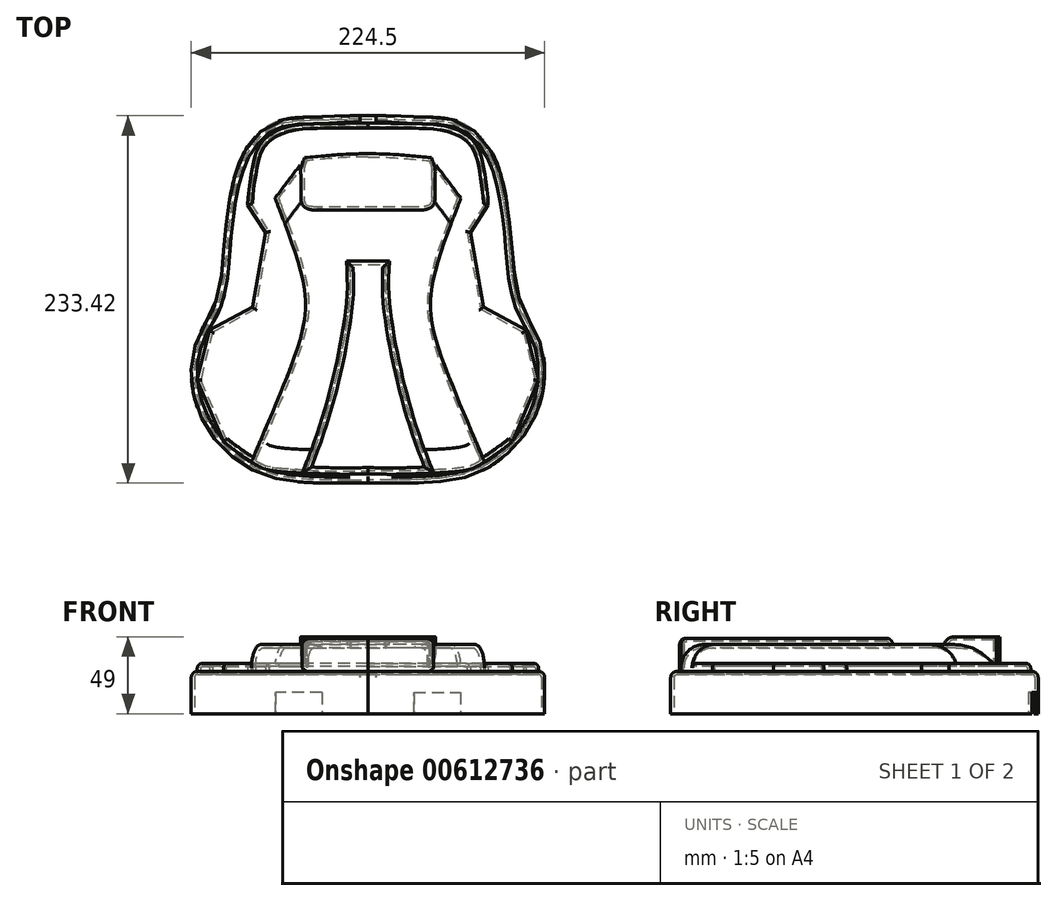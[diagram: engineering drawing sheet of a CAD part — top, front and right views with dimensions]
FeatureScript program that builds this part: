
annotation { "Feature Type Name" : "Feature", "Feature Type Description" : "" }
export const myFeature = defineFeature(function(context is Context, id is Id, definition is map)
    precondition{}
    {
        {
            var Q0;
            Q0=qCreatedBy(makeId("Top.planeOp"),FACE);
            var sketch = newSketch(context, id + "F0", { "sketchPlane" : qUnion([Q0])});
            skFitSpline(sketch, "E0", {"points": [v(0, 119.05) * mm, v(-30.72, 118.24) * mm, v(-55.15, 116.1) * mm, v(-69.4, 106.9) * mm, v(-80.35, 89.32) * mm, v(-88.63, 47.3) * mm, v(-91.91, 14.02) * mm, v(-96.74, -3.06) * mm, v(-101.1, -10.8) * mm, v(-108.33, -26.62) * mm, v(-110.21, -43.05) * mm, v(-107.64, -60) * mm, v(-100.19, -76.77) * mm, v(-92.8, -86.72) * mm, v(-84.5, -94.37) * mm, v(-62.4, -106.34) * mm, v(0, -110.2) * mm], "startDerivative": vector(-744.36, 0) * mm, "endDerivative": vector(685.33, 9.02) * mm});
            skFitSpline(sketch, "E1.MirrorCS", {"points": [v(0, 119.05) * mm, v(30.72, 118.24) * mm, v(55.15, 116.1) * mm, v(69.4, 106.9) * mm, v(80.35, 89.32) * mm, v(88.63, 47.3) * mm, v(91.91, 14.02) * mm, v(96.74, -3.06) * mm, v(101.1, -10.8) * mm, v(108.33, -26.62) * mm, v(110.21, -43.05) * mm, v(107.64, -60) * mm, v(100.19, -76.77) * mm, v(92.8, -86.72) * mm, v(84.5, -94.37) * mm, v(62.4, -106.34) * mm, v(0, -110.2) * mm], "startDerivative": vector(744.36, 0) * mm, "endDerivative": vector(-685.33, 9.02) * mm});
            skLineSegment(sketch, "E2", {"start": v(-4.96, 119.03) * mm, "end": v(4.96, 119.03) * mm});
            skLineSegment(sketch, "E3", {"start": v(-11.45, -110.35) * mm, "end": v(15, -110.37) * mm});
            skFitSpline(sketch, "E4", {"points": [v(0, 114.28) * mm, v(-18.36, 114.15) * mm, v(-47.6, 112.7) * mm, v(-55.77, 110.2) * mm, v(-60.12, 108.09) * mm, v(-67.36, 100.84) * mm, v(-71.66, 86.85) * mm, v(-74.01, 70.56) * mm, v(-74.33, 64.92) * mm], "startDerivative": vector(-107.9, -0.71) * mm, "endDerivative": vector(-1.45, -57.59) * mm});
            skFitSpline(sketch, "E5", {"points": [v(-74.33, 64.92) * mm, v(-62.9, 47.38) * mm], "startDerivative": vector(11.44, -17.55) * mm, "endDerivative": vector(11.44, -17.55) * mm});
            skFitSpline(sketch, "E6", {"points": [v(-62.9, 47.38) * mm, v(-71.5, -1.86) * mm], "startDerivative": vector(-8.62, -49.24) * mm, "endDerivative": vector(-8.62, -49.24) * mm});
            skFitSpline(sketch, "E7", {"points": [v(-71.5, -1.86) * mm, v(-98.76, -16.48) * mm], "startDerivative": vector(-27.25, -14.62) * mm, "endDerivative": vector(-27.25, -14.62) * mm});
            skFitSpline(sketch, "E8", {"points": [v(-98.76, -16.48) * mm, v(-106.3, -46.83) * mm], "startDerivative": vector(-7.53, -30.35) * mm, "endDerivative": vector(-7.53, -30.35) * mm});
            skFitSpline(sketch, "E9", {"points": [v(-106.3, -46.83) * mm, v(-90.12, -84.72) * mm], "startDerivative": vector(16.17, -37.88) * mm, "endDerivative": vector(16.17, -37.88) * mm});
            skFitSpline(sketch, "E10", {"points": [v(-90.12, -84.72) * mm, v(-84.53, -89.16) * mm, v(-71.5, -98) * mm, v(-62.4, -102.03) * mm, v(-36.71, -104.14) * mm, v(-18.66, -104.7) * mm, v(0, -104.51) * mm], "startDerivative": vector(41.41, -35.24) * mm, "endDerivative": vector(104.18, 2) * mm});
            skFitSpline(sketch, "E11", {"points": [v(0, 94.84) * mm, v(-38.88, 92.49) * mm], "startDerivative": vector(-38.9, 0.44) * mm, "endDerivative": vector(-38.29, -3.6) * mm});
            skFitSpline(sketch, "E12", {"points": [v(-38.88, 92.49) * mm, v(-56.85, 68.63) * mm], "startDerivative": vector(-17.94, -24.15) * mm, "endDerivative": vector(-17.94, -24.15) * mm});
            skFitSpline(sketch, "E13", {"points": [v(-56.85, 68.63) * mm, v(-38.88, 14.12) * mm, v(-38.88, -11.88) * mm, v(-45.96, -36) * mm, v(-60.7, -72.63) * mm, v(-71.5, -98) * mm], "startDerivative": vector(88.21, -228.17) * mm, "endDerivative": vector(-56.6, -131.92) * mm});
            skFitSpline(sketch, "E14", {"points": [v(-38.88, -104.14) * mm, v(-28.8, -76.77) * mm, v(-18.16, -36.98) * mm, v(-11.45, 5.1) * mm, v(-11.45, 26.6) * mm], "startDerivative": vector(43.74, 111.22) * mm, "endDerivative": vector(-4.53, 97.24) * mm});
            skFitSpline(sketch, "E15", {"points": [v(-11.45, 26.6) * mm, v(0, 26.6) * mm], "startDerivative": vector(11.45, 0) * mm, "endDerivative": vector(11.45, 0) * mm});
            skFitSpline(sketch, "E16.MirrorCS", {"points": [v(11.45, 26.6) * mm, v(0, 26.6) * mm], "startDerivative": vector(-11.45, 0) * mm, "endDerivative": vector(-11.45, 0) * mm});
            skFitSpline(sketch, "E17.MirrorCS", {"points": [v(106.3, -46.83) * mm, v(90.12, -84.72) * mm], "startDerivative": vector(-16.17, -37.88) * mm, "endDerivative": vector(-16.17, -37.88) * mm});
            skFitSpline(sketch, "E18.MirrorCS", {"points": [v(0, 94.84) * mm, v(38.88, 92.49) * mm], "startDerivative": vector(38.9, 0.44) * mm, "endDerivative": vector(38.29, -3.6) * mm});
            skFitSpline(sketch, "E19.MirrorCS", {"points": [v(38.88, 92.49) * mm, v(56.85, 68.63) * mm], "startDerivative": vector(17.94, -24.15) * mm, "endDerivative": vector(17.94, -24.15) * mm});
            skFitSpline(sketch, "E20.MirrorCS", {"points": [v(98.76, -16.48) * mm, v(106.3, -46.83) * mm], "startDerivative": vector(7.53, -30.35) * mm, "endDerivative": vector(7.53, -30.35) * mm});
            skFitSpline(sketch, "E21.MirrorCS", {"points": [v(74.33, 64.92) * mm, v(62.9, 47.38) * mm], "startDerivative": vector(-11.44, -17.55) * mm, "endDerivative": vector(-11.44, -17.55) * mm});
            skFitSpline(sketch, "E22.MirrorCS", {"points": [v(62.9, 47.38) * mm, v(71.5, -1.86) * mm], "startDerivative": vector(8.62, -49.24) * mm, "endDerivative": vector(8.62, -49.24) * mm});
            skFitSpline(sketch, "E23.MirrorCS", {"points": [v(71.5, -1.86) * mm, v(98.76, -16.48) * mm], "startDerivative": vector(27.25, -14.62) * mm, "endDerivative": vector(27.25, -14.62) * mm});
            skFitSpline(sketch, "E24.MirrorCS", {"points": [v(38.88, -104.14) * mm, v(28.8, -76.77) * mm, v(18.16, -36.98) * mm, v(11.45, 5.1) * mm, v(11.45, 26.6) * mm], "startDerivative": vector(-43.74, 111.22) * mm, "endDerivative": vector(4.53, 97.24) * mm});
            skFitSpline(sketch, "E25.MirrorCS", {"points": [v(90.12, -84.72) * mm, v(84.53, -89.16) * mm, v(71.5, -98) * mm, v(62.4, -102.03) * mm, v(36.71, -104.14) * mm, v(18.66, -104.7) * mm, v(0, -104.51) * mm], "startDerivative": vector(-41.41, -35.24) * mm, "endDerivative": vector(-104.18, 2) * mm});
            skFitSpline(sketch, "E26.MirrorCS", {"points": [v(0, 114.28) * mm, v(18.36, 114.15) * mm, v(47.6, 112.7) * mm, v(55.77, 110.2) * mm, v(60.12, 108.09) * mm, v(67.36, 100.84) * mm, v(71.66, 86.85) * mm, v(74.01, 70.56) * mm, v(74.33, 64.92) * mm], "startDerivative": vector(107.9, -0.71) * mm, "endDerivative": vector(1.45, -57.59) * mm});
            skFitSpline(sketch, "E27.MirrorCS", {"points": [v(56.85, 68.63) * mm, v(38.88, 14.12) * mm, v(38.88, -11.88) * mm, v(45.96, -36) * mm, v(60.7, -72.63) * mm, v(71.5, -98) * mm], "startDerivative": vector(-88.21, -228.17) * mm, "endDerivative": vector(56.6, -131.92) * mm});
            skFitSpline(sketch, "E28", {"points": [v(-38.88, 92.49) * mm, v(-40.62, 87.48) * mm, v(-40.62, 82.08) * mm, v(-40.62, 69.41) * mm, v(-38.88, 64.38) * mm, v(-28.7, 62.89) * mm], "startDerivative": vector(-12.59, -32.74) * mm, "endDerivative": vector(53.36, -0.8) * mm});
            skFitSpline(sketch, "E29", {"points": [v(-28.7, 62.89) * mm, v(0, 62.89) * mm], "startDerivative": vector(28.7, 0) * mm, "endDerivative": vector(28.7, 0) * mm});
            skFitSpline(sketch, "E30", {"points": [v(-50.82, 52.88) * mm, v(-38.88, 50.97) * mm, v(-9.51, 48.92) * mm, v(0, 48.92) * mm], "startDerivative": vector(50.24, -10.28) * mm, "endDerivative": vector(115.6, -0.34) * mm});
            skFitSpline(sketch, "E31.MirrorCS", {"points": [v(38.88, 92.49) * mm, v(40.62, 87.48) * mm, v(40.62, 82.08) * mm, v(40.62, 69.41) * mm, v(38.88, 64.38) * mm, v(28.7, 62.89) * mm], "startDerivative": vector(12.59, -32.74) * mm, "endDerivative": vector(-53.36, -0.8) * mm});
            skFitSpline(sketch, "E32.MirrorCS", {"points": [v(28.7, 62.89) * mm, v(0, 62.89) * mm], "startDerivative": vector(-28.7, 0) * mm, "endDerivative": vector(-28.7, 0) * mm});
            skFitSpline(sketch, "E33.MirrorCS", {"points": [v(50.82, 52.88) * mm, v(38.88, 50.97) * mm, v(9.51, 48.92) * mm, v(0, 48.92) * mm], "startDerivative": vector(-50.24, -10.28) * mm, "endDerivative": vector(-115.6, -0.34) * mm});
            skSolve(sketch);
        }
        {
            var Q0;
            {var subQ6=sQuery(id+"F0.wireOp",EDGE,"E15");Q0=makeQuery(id+"F0.imprint","IMPRINT",FACE,{"disambiguationData":[TD([[makeQuery(id+"F0.imprint","IMPRINT",EDGE,{"derivedFrom":subQ6}),-1.0]])]});}
            extrude(context, id + "F1", {"entities" : qUnion([Q0]), "depth" : 46 * mm, "offsetDistance" : 25 * mm});
        }
        {
            var Q0;
            {var subQ0=sQuery(id+"F0.wireOp",EDGE,"E15");Q0=makeQuery(id+"F0.imprint","IMPRINT",FACE,{"disambiguationData":[TD([[makeQuery(id+"F0.imprint","IMPRINT",EDGE,{"derivedFrom":subQ0}),1.0]])]});}
            extrude(context, id + "F2", {"entities" : qUnion([Q0]), "operationType" : NewBodyOperationType.ADD, "depth" : 42 * mm, "offsetDistance" : 25 * mm});
        }
        {
            var Q0;
            Q0=makeQuery(id+"F0.imprint","IMPRINT",FACE,{"disambiguationData":[TD([[makeQuery(id+"F0.imprint","IMPRINT",EDGE,{"derivedFrom":sQuery(id+"F0.wireOp",EDGE,"E4")}),1.0]])]});
            extrude(context, id + "F3", {"entities" : qUnion([Q0]), "operationType" : NewBodyOperationType.ADD, "depth" : 30 * mm, "offsetDistance" : 25 * mm});
        }
        {
            var Q0;
            {var subQ11=sQuery(id+"F0.wireOp",EDGE,"E2");Q0=makeQuery(id+"F0.imprint","IMPRINT",FACE,{"disambiguationData":[TD([[makeQuery(id+"F0.imprint","IMPRINT",EDGE,{"derivedFrom":subQ11}),-1.0]])]});}
            extrude(context, id + "F4", {"entities" : qUnion([Q0]), "operationType" : NewBodyOperationType.ADD, "depth" : 25 * mm, "offsetDistance" : 25 * mm});
        }
        {
            var Q0;
            Q0=makeQuery(id+"F0.imprint","IMPRINT",FACE,{"disambiguationData":[TD([[makeQuery(id+"F0.imprint","IMPRINT",EDGE,{"derivedFrom":sQuery(id+"F0.wireOp",EDGE,"E11")}),1.0]])]});
            extrude(context, id + "F5", {"entities" : qUnion([Q0]), "operationType" : NewBodyOperationType.ADD, "depth" : 47 * mm, "offsetDistance" : 25 * mm});
        }
        {
            var Q0;
            {var subQ4=sQuery(id+"F0.wireOp",EDGE,"E12");Q0=makeQuery(id+"F0.imprint","IMPRINT",FACE,{"disambiguationData":[TD([[makeQuery(id+"F0.imprint","IMPRINT",EDGE,{"derivedFrom":subQ4}),1.0]])]});}
            extrude(context, id + "F6", {"entities" : qUnion([Q0]), "operationType" : NewBodyOperationType.ADD, "depth" : 42 * mm, "offsetDistance" : 25 * mm});
        }
        {
            var Q0;
            Q0=makeQuery(id+"F1.opExtrude","CAP_EDGE",EDGE,{"disambiguationData":[OSD([sQuery(id+"F0.wireOp",EDGE,"E14")])],"isStart":false});
            var Q1;
            Q1=makeQuery(id+"F1.opExtrude","CAP_EDGE",EDGE,{"disambiguationData":[OSD([sQuery(id+"F0.wireOp",EDGE,"E24.MirrorCS")])],"isStart":false});
            var Q2;
            Q2=makeQuery(id+"F1.opExtrude","CAP_FACE",FACE,{"disambiguationData":[OSD([sQuery(id+"F0.wireOp",EDGE,"E10"),sQuery(id+"F0.wireOp",EDGE,"E14"),sQuery(id+"F0.wireOp",EDGE,"E15"),sQuery(id+"F0.wireOp",EDGE,"E16.MirrorCS"),sQuery(id+"F0.wireOp",EDGE,"E24.MirrorCS"),sQuery(id+"F0.wireOp",EDGE,"E25.MirrorCS")])],"isStart":false});
            fillet(context, id + "F7", {"entities" : qUnion([Q0, Q1, Q2]), "radius" : 2 * mm, "tangentPropagation" : true, "allowEdgeOverflow" : false});
        }
        {
            var Q0;
            Q0=makeQuery(id+"F5.opExtrude","CAP_EDGE",EDGE,{"disambiguationData":[OSD([sQuery(id+"F0.wireOp",EDGE,"E32.MirrorCS")])],"isStart":false});
            var Q1;
            Q1=makeQuery(id+"F5.opExtrude","CAP_EDGE",EDGE,{"disambiguationData":[OSD([sQuery(id+"F0.wireOp",EDGE,"E29")])],"isStart":false});
            fillet(context, id + "F8", {"entities" : qUnion([Q0, Q1]), "radius" : 5 * mm, "tangentPropagation" : true, "allowEdgeOverflow" : false});
        }
        {
            var Q0;
            {var subQ0=sQuery(id+"F0.wireOp",EDGE,"E13");Q0=makeQuery(id+"F6.boolean.opBoolean","MERGE",EDGE,{"derivedFrom":[makeQuery(id+"F2.opExtrude","CAP_EDGE",EDGE,{"disambiguationData":[OSD([subQ0])],"isStart":false}),makeQuery(id+"F6.opExtrude","CAP_EDGE",EDGE,{"disambiguationData":[OSD([subQ0])],"isStart":false})]});}
            var Q1;
            Q1=makeQuery(id+"F6.opExtrude","CAP_EDGE",EDGE,{"disambiguationData":[OSD([sQuery(id+"F0.wireOp",EDGE,"E12")])],"isStart":false});
            var Q2;
            Q2=makeQuery(id+"F6.opExtrude","CAP_EDGE",EDGE,{"disambiguationData":[OSD([sQuery(id+"F0.wireOp",EDGE,"E19.MirrorCS")])],"isStart":false});
            var Q3;
            {var subQ0=sQuery(id+"F0.wireOp",EDGE,"E27.MirrorCS");Q3=makeQuery(id+"F6.boolean.opBoolean","MERGE",EDGE,{"derivedFrom":[makeQuery(id+"F2.opExtrude","CAP_EDGE",EDGE,{"disambiguationData":[OSD([subQ0])],"isStart":false}),makeQuery(id+"F6.opExtrude","CAP_EDGE",EDGE,{"disambiguationData":[OSD([subQ0])],"isStart":false})]});}
            var Q4;
            Q4=makeQuery(id+"F2.opExtrude","CAP_EDGE",EDGE,{"disambiguationData":[OSD([sQuery(id+"F0.wireOp",EDGE,"E25.MirrorCS")])],"isStart":false});
            var Q5;
            Q5=makeQuery(id+"F2.opExtrude","CAP_EDGE",EDGE,{"disambiguationData":[OSD([sQuery(id+"F0.wireOp",EDGE,"E10")])],"isStart":false});
            fillet(context, id + "F9", {"entities" : qUnion([Q0, Q1, Q2, Q3, Q4, Q5]), "radius" : 13 * mm, "tangentPropagation" : true, "allowEdgeOverflow" : false});
        }
        {
            var Q0;
            Q0=makeQuery(id+"F3.opExtrude","CAP_EDGE",EDGE,{"disambiguationData":[OSD([sQuery(id+"F0.wireOp",EDGE,"E9")])],"isStart":false});
            var Q1;
            {var subQ0=sQuery(id+"F0.wireOp",EDGE,"E10");Q1=makeQuery(id+"F9.opFillet","BLEND_EDGE",EDGE,{"blendedFrom":[makeQuery(id+"F2.opExtrude","CAP_EDGE",EDGE,{"disambiguationData":[OSD([subQ0])],"isStart":false}),makeQuery(id+"F3.opExtrude","CAP_FACE",FACE,{"disambiguationData":[OSD([sQuery(id+"F0.wireOp",EDGE,"E4"),sQuery(id+"F0.wireOp",EDGE,"E5"),sQuery(id+"F0.wireOp",EDGE,"E6"),sQuery(id+"F0.wireOp",EDGE,"E7"),sQuery(id+"F0.wireOp",EDGE,"E8"),sQuery(id+"F0.wireOp",EDGE,"E9"),subQ0,sQuery(id+"F0.wireOp",EDGE,"E11"),sQuery(id+"F0.wireOp",EDGE,"E12"),sQuery(id+"F0.wireOp",EDGE,"E13"),sQuery(id+"F0.wireOp",EDGE,"E17.MirrorCS"),sQuery(id+"F0.wireOp",EDGE,"E18.MirrorCS"),sQuery(id+"F0.wireOp",EDGE,"E19.MirrorCS"),sQuery(id+"F0.wireOp",EDGE,"E20.MirrorCS"),sQuery(id+"F0.wireOp",EDGE,"E21.MirrorCS"),sQuery(id+"F0.wireOp",EDGE,"E22.MirrorCS"),sQuery(id+"F0.wireOp",EDGE,"E23.MirrorCS"),sQuery(id+"F0.wireOp",EDGE,"E25.MirrorCS"),sQuery(id+"F0.wireOp",EDGE,"E26.MirrorCS"),sQuery(id+"F0.wireOp",EDGE,"E27.MirrorCS")])],"isStart":false})],"blendedInto":[makeQuery(id+"F3.opExtrude","CAP_FACE",FACE,{"disambiguationData":[OSD([sQuery(id+"F0.wireOp",EDGE,"E4"),sQuery(id+"F0.wireOp",EDGE,"E5"),sQuery(id+"F0.wireOp",EDGE,"E6"),sQuery(id+"F0.wireOp",EDGE,"E7"),sQuery(id+"F0.wireOp",EDGE,"E8"),sQuery(id+"F0.wireOp",EDGE,"E9"),subQ0,sQuery(id+"F0.wireOp",EDGE,"E11"),sQuery(id+"F0.wireOp",EDGE,"E12"),sQuery(id+"F0.wireOp",EDGE,"E13"),sQuery(id+"F0.wireOp",EDGE,"E17.MirrorCS"),sQuery(id+"F0.wireOp",EDGE,"E18.MirrorCS"),sQuery(id+"F0.wireOp",EDGE,"E19.MirrorCS"),sQuery(id+"F0.wireOp",EDGE,"E20.MirrorCS"),sQuery(id+"F0.wireOp",EDGE,"E21.MirrorCS"),sQuery(id+"F0.wireOp",EDGE,"E22.MirrorCS"),sQuery(id+"F0.wireOp",EDGE,"E23.MirrorCS"),sQuery(id+"F0.wireOp",EDGE,"E25.MirrorCS"),sQuery(id+"F0.wireOp",EDGE,"E26.MirrorCS"),sQuery(id+"F0.wireOp",EDGE,"E27.MirrorCS")])],"isStart":false})]});}
            var Q2;
            Q2=makeQuery(id+"F3.opExtrude","CAP_EDGE",EDGE,{"disambiguationData":[OSD([sQuery(id+"F0.wireOp",EDGE,"E8")])],"isStart":false});
            var Q3;
            Q3=makeQuery(id+"F3.opExtrude","CAP_EDGE",EDGE,{"disambiguationData":[OSD([sQuery(id+"F0.wireOp",EDGE,"E7")])],"isStart":false});
            var Q4;
            Q4=makeQuery(id+"F3.opExtrude","CAP_EDGE",EDGE,{"disambiguationData":[OSD([sQuery(id+"F0.wireOp",EDGE,"E6")])],"isStart":false});
            var Q5;
            Q5=makeQuery(id+"F3.opExtrude","CAP_EDGE",EDGE,{"disambiguationData":[OSD([sQuery(id+"F0.wireOp",EDGE,"E5")])],"isStart":false});
            var Q6;
            Q6=makeQuery(id+"F3.opExtrude","CAP_EDGE",EDGE,{"disambiguationData":[OSD([sQuery(id+"F0.wireOp",EDGE,"E4")])],"isStart":false});
            var Q7;
            Q7=makeQuery(id+"F3.opExtrude","CAP_EDGE",EDGE,{"disambiguationData":[OSD([sQuery(id+"F0.wireOp",EDGE,"E26.MirrorCS")])],"isStart":false});
            var Q8;
            Q8=makeQuery(id+"F3.opExtrude","CAP_EDGE",EDGE,{"disambiguationData":[OSD([sQuery(id+"F0.wireOp",EDGE,"E21.MirrorCS")])],"isStart":false});
            var Q9;
            Q9=makeQuery(id+"F3.opExtrude","CAP_EDGE",EDGE,{"disambiguationData":[OSD([sQuery(id+"F0.wireOp",EDGE,"E22.MirrorCS")])],"isStart":false});
            var Q10;
            Q10=makeQuery(id+"F3.opExtrude","CAP_EDGE",EDGE,{"disambiguationData":[OSD([sQuery(id+"F0.wireOp",EDGE,"E23.MirrorCS")])],"isStart":false});
            var Q11;
            Q11=makeQuery(id+"F3.opExtrude","CAP_EDGE",EDGE,{"disambiguationData":[OSD([sQuery(id+"F0.wireOp",EDGE,"E20.MirrorCS")])],"isStart":false});
            var Q12;
            Q12=makeQuery(id+"F3.opExtrude","CAP_EDGE",EDGE,{"disambiguationData":[OSD([sQuery(id+"F0.wireOp",EDGE,"E17.MirrorCS")])],"isStart":false});
            var Q13;
            {var subQ0=sQuery(id+"F0.wireOp",EDGE,"E25.MirrorCS");Q13=makeQuery(id+"F9.opFillet","BLEND_EDGE",EDGE,{"blendedFrom":[makeQuery(id+"F2.opExtrude","CAP_EDGE",EDGE,{"disambiguationData":[OSD([subQ0])],"isStart":false}),makeQuery(id+"F3.opExtrude","CAP_FACE",FACE,{"disambiguationData":[OSD([sQuery(id+"F0.wireOp",EDGE,"E4"),sQuery(id+"F0.wireOp",EDGE,"E5"),sQuery(id+"F0.wireOp",EDGE,"E6"),sQuery(id+"F0.wireOp",EDGE,"E7"),sQuery(id+"F0.wireOp",EDGE,"E8"),sQuery(id+"F0.wireOp",EDGE,"E9"),sQuery(id+"F0.wireOp",EDGE,"E10"),sQuery(id+"F0.wireOp",EDGE,"E11"),sQuery(id+"F0.wireOp",EDGE,"E12"),sQuery(id+"F0.wireOp",EDGE,"E13"),sQuery(id+"F0.wireOp",EDGE,"E17.MirrorCS"),sQuery(id+"F0.wireOp",EDGE,"E18.MirrorCS"),sQuery(id+"F0.wireOp",EDGE,"E19.MirrorCS"),sQuery(id+"F0.wireOp",EDGE,"E20.MirrorCS"),sQuery(id+"F0.wireOp",EDGE,"E21.MirrorCS"),sQuery(id+"F0.wireOp",EDGE,"E22.MirrorCS"),sQuery(id+"F0.wireOp",EDGE,"E23.MirrorCS"),subQ0,sQuery(id+"F0.wireOp",EDGE,"E26.MirrorCS"),sQuery(id+"F0.wireOp",EDGE,"E27.MirrorCS")])],"isStart":false})],"blendedInto":[makeQuery(id+"F3.opExtrude","CAP_FACE",FACE,{"disambiguationData":[OSD([sQuery(id+"F0.wireOp",EDGE,"E4"),sQuery(id+"F0.wireOp",EDGE,"E5"),sQuery(id+"F0.wireOp",EDGE,"E6"),sQuery(id+"F0.wireOp",EDGE,"E7"),sQuery(id+"F0.wireOp",EDGE,"E8"),sQuery(id+"F0.wireOp",EDGE,"E9"),sQuery(id+"F0.wireOp",EDGE,"E10"),sQuery(id+"F0.wireOp",EDGE,"E11"),sQuery(id+"F0.wireOp",EDGE,"E12"),sQuery(id+"F0.wireOp",EDGE,"E13"),sQuery(id+"F0.wireOp",EDGE,"E17.MirrorCS"),sQuery(id+"F0.wireOp",EDGE,"E18.MirrorCS"),sQuery(id+"F0.wireOp",EDGE,"E19.MirrorCS"),sQuery(id+"F0.wireOp",EDGE,"E20.MirrorCS"),sQuery(id+"F0.wireOp",EDGE,"E21.MirrorCS"),sQuery(id+"F0.wireOp",EDGE,"E22.MirrorCS"),sQuery(id+"F0.wireOp",EDGE,"E23.MirrorCS"),subQ0,sQuery(id+"F0.wireOp",EDGE,"E26.MirrorCS"),sQuery(id+"F0.wireOp",EDGE,"E27.MirrorCS")])],"isStart":false})]});}
            fillet(context, id + "F10", {"entities" : qUnion([Q0, Q1, Q2, Q3, Q4, Q5, Q6, Q7, Q8, Q9, Q10, Q11, Q12, Q13]), "radius" : 1 * mm, "tangentPropagation" : true, "allowEdgeOverflow" : false});
        }
        {
            var Q0;
            Q0=makeQuery(id+"F4.opExtrude","CAP_EDGE",EDGE,{"disambiguationData":[OSD([sQuery(id+"F0.wireOp",EDGE,"E1.MirrorCS")])],"isStart":false});
            var Q1;
            Q1=makeQuery(id+"F4.opExtrude","CAP_EDGE",EDGE,{"disambiguationData":[OSD([sQuery(id+"F0.wireOp",EDGE,"E0")])],"isStart":false});
            var Q2;
            Q2=makeQuery(id+"F4.opExtrude","CAP_EDGE",EDGE,{"disambiguationData":[OSD([sQuery(id+"F0.wireOp",EDGE,"E2")])],"isStart":false});
            fillet(context, id + "F11", {"entities" : qUnion([Q0, Q1, Q2]), "radius" : 2 * mm, "tangentPropagation" : true, "allowEdgeOverflow" : false});
        }
        {
            var Q0;
            {var subQ0=sQuery(id+"F0.wireOp",EDGE,"E33.MirrorCS");var subQ1=sQuery(id+"F0.wireOp",EDGE,"E32.MirrorCS");var subQ2=sQuery(id+"F0.wireOp",EDGE,"E31.MirrorCS");var subQ3=sQuery(id+"F0.wireOp",EDGE,"E30");var subQ4=sQuery(id+"F0.wireOp",EDGE,"E29");var subQ5=sQuery(id+"F0.wireOp",EDGE,"E28");var subQ6=sQuery(id+"F0.wireOp",EDGE,"E27.MirrorCS");var subQ7=sQuery(id+"F0.wireOp",EDGE,"E19.MirrorCS");var subQ8=sQuery(id+"F0.wireOp",EDGE,"E13");var subQ9=sQuery(id+"F0.wireOp",EDGE,"E12");var subQ10=sQuery(id+"F0.wireOp",EDGE,"E18.MirrorCS");var subQ11=sQuery(id+"F0.wireOp",EDGE,"E11");var subQ12=sQuery(id+"F0.wireOp",EDGE,"E26.MirrorCS");var subQ13=sQuery(id+"F0.wireOp",EDGE,"E25.MirrorCS");var subQ14=sQuery(id+"F0.wireOp",EDGE,"E23.MirrorCS");var subQ15=sQuery(id+"F0.wireOp",EDGE,"E22.MirrorCS");var subQ16=sQuery(id+"F0.wireOp",EDGE,"E21.MirrorCS");var subQ17=sQuery(id+"F0.wireOp",EDGE,"E20.MirrorCS");var subQ18=sQuery(id+"F0.wireOp",EDGE,"E17.MirrorCS");var subQ19=sQuery(id+"F0.wireOp",EDGE,"E10");var subQ20=sQuery(id+"F0.wireOp",EDGE,"E9");var subQ21=sQuery(id+"F0.wireOp",EDGE,"E8");var subQ22=sQuery(id+"F0.wireOp",EDGE,"E7");var subQ23=sQuery(id+"F0.wireOp",EDGE,"E6");var subQ24=sQuery(id+"F0.wireOp",EDGE,"E5");var subQ25=sQuery(id+"F0.wireOp",EDGE,"E4");var subQ26=sQuery(id+"F0.wireOp",EDGE,"E24.MirrorCS");var subQ27=sQuery(id+"F0.wireOp",EDGE,"E16.MirrorCS");var subQ28=sQuery(id+"F0.wireOp",EDGE,"E15");var subQ29=sQuery(id+"F0.wireOp",EDGE,"E14");Q0=makeQuery(id+"F6.boolean.opBoolean","MERGE",FACE,{"derivedFrom":[makeQuery(id+"F5.boolean.opBoolean","MERGE",FACE,{"derivedFrom":[makeQuery(id+"F4.boolean.opBoolean","MERGE",FACE,{"derivedFrom":[makeQuery(id+"F3.boolean.opBoolean","MERGE",FACE,{"derivedFrom":[makeQuery(id+"F2.boolean.opBoolean","MERGE",FACE,{"derivedFrom":[makeQuery(id+"F1.opExtrude","CAP_FACE",FACE,{"disambiguationData":[OSD([subQ19,subQ29,subQ28,subQ27,subQ26,subQ13])],"isStart":true}),makeQuery(id+"F2.opExtrude","CAP_FACE",FACE,{"disambiguationData":[OSD([subQ19,subQ8,subQ29,subQ28,subQ27,subQ26,subQ13,subQ6,subQ3,subQ0])],"isStart":true})]}),makeQuery(id+"F3.opExtrude","CAP_FACE",FACE,{"disambiguationData":[OSD([subQ25,subQ24,subQ23,subQ22,subQ21,subQ20,subQ19,subQ11,subQ9,subQ8,subQ18,subQ10,subQ7,subQ17,subQ16,subQ15,subQ14,subQ13,subQ12,subQ6])],"isStart":true})]}),makeQuery(id+"F4.opExtrude","CAP_FACE",FACE,{"disambiguationData":[OSD([sQuery(id+"F0.wireOp",EDGE,"E0"),sQuery(id+"F0.wireOp",EDGE,"E1.MirrorCS"),sQuery(id+"F0.wireOp",EDGE,"E2"),subQ25,subQ24,subQ23,subQ22,subQ21,subQ20,subQ19,subQ18,subQ17,subQ16,subQ15,subQ14,subQ13,subQ12])],"isStart":true})]}),makeQuery(id+"F5.opExtrude","CAP_FACE",FACE,{"disambiguationData":[OSD([subQ11,subQ10,subQ5,subQ4,subQ2,subQ1])],"isStart":true})]}),makeQuery(id+"F6.opExtrude","CAP_FACE",FACE,{"disambiguationData":[OSD([subQ9,subQ8,subQ7,subQ6,subQ5,subQ4,subQ3,subQ2,subQ1,subQ0])],"isStart":true})]});}
            shell(context, id + "F12", {"entities" : qUnion([Q0]), "thickness" : 2 * mm, "oppositeDirection" : true});
        }
        {
            var Q0;
            {var subQ0=sQuery(id+"F0.wireOp",EDGE,"E33.MirrorCS");var subQ1=sQuery(id+"F0.wireOp",EDGE,"E32.MirrorCS");var subQ2=sQuery(id+"F0.wireOp",EDGE,"E31.MirrorCS");var subQ3=sQuery(id+"F0.wireOp",EDGE,"E30");var subQ4=sQuery(id+"F0.wireOp",EDGE,"E29");var subQ5=sQuery(id+"F0.wireOp",EDGE,"E28");var subQ6=sQuery(id+"F0.wireOp",EDGE,"E27.MirrorCS");var subQ7=sQuery(id+"F0.wireOp",EDGE,"E19.MirrorCS");var subQ8=sQuery(id+"F0.wireOp",EDGE,"E13");var subQ9=sQuery(id+"F0.wireOp",EDGE,"E12");var subQ10=sQuery(id+"F0.wireOp",EDGE,"E18.MirrorCS");var subQ11=sQuery(id+"F0.wireOp",EDGE,"E11");var subQ12=sQuery(id+"F0.wireOp",EDGE,"E26.MirrorCS");var subQ13=sQuery(id+"F0.wireOp",EDGE,"E25.MirrorCS");var subQ14=sQuery(id+"F0.wireOp",EDGE,"E23.MirrorCS");var subQ15=sQuery(id+"F0.wireOp",EDGE,"E22.MirrorCS");var subQ16=sQuery(id+"F0.wireOp",EDGE,"E21.MirrorCS");var subQ17=sQuery(id+"F0.wireOp",EDGE,"E20.MirrorCS");var subQ18=sQuery(id+"F0.wireOp",EDGE,"E17.MirrorCS");var subQ19=sQuery(id+"F0.wireOp",EDGE,"E10");var subQ20=sQuery(id+"F0.wireOp",EDGE,"E9");var subQ21=sQuery(id+"F0.wireOp",EDGE,"E8");var subQ22=sQuery(id+"F0.wireOp",EDGE,"E7");var subQ23=sQuery(id+"F0.wireOp",EDGE,"E6");var subQ24=sQuery(id+"F0.wireOp",EDGE,"E5");var subQ25=sQuery(id+"F0.wireOp",EDGE,"E4");var subQ26=sQuery(id+"F0.wireOp",EDGE,"E24.MirrorCS");var subQ27=sQuery(id+"F0.wireOp",EDGE,"E16.MirrorCS");var subQ28=sQuery(id+"F0.wireOp",EDGE,"E15");var subQ29=sQuery(id+"F0.wireOp",EDGE,"E14");Q0=makeQuery(id+"F6.boolean.opBoolean","MERGE",FACE,{"derivedFrom":[makeQuery(id+"F5.boolean.opBoolean","MERGE",FACE,{"derivedFrom":[makeQuery(id+"F4.boolean.opBoolean","MERGE",FACE,{"derivedFrom":[makeQuery(id+"F3.boolean.opBoolean","MERGE",FACE,{"derivedFrom":[makeQuery(id+"F2.boolean.opBoolean","MERGE",FACE,{"derivedFrom":[makeQuery(id+"F1.opExtrude","CAP_FACE",FACE,{"disambiguationData":[OSD([subQ19,subQ29,subQ28,subQ27,subQ26,subQ13])],"isStart":true}),makeQuery(id+"F2.opExtrude","CAP_FACE",FACE,{"disambiguationData":[OSD([subQ19,subQ8,subQ29,subQ28,subQ27,subQ26,subQ13,subQ6,subQ3,subQ0])],"isStart":true})]}),makeQuery(id+"F3.opExtrude","CAP_FACE",FACE,{"disambiguationData":[OSD([subQ25,subQ24,subQ23,subQ22,subQ21,subQ20,subQ19,subQ11,subQ9,subQ8,subQ18,subQ10,subQ7,subQ17,subQ16,subQ15,subQ14,subQ13,subQ12,subQ6])],"isStart":true})]}),makeQuery(id+"F4.opExtrude","CAP_FACE",FACE,{"disambiguationData":[OSD([sQuery(id+"F0.wireOp",EDGE,"E0"),sQuery(id+"F0.wireOp",EDGE,"E1.MirrorCS"),sQuery(id+"F0.wireOp",EDGE,"E2"),subQ25,subQ24,subQ23,subQ22,subQ21,subQ20,subQ19,subQ18,subQ17,subQ16,subQ15,subQ14,subQ13,subQ12])],"isStart":true})]}),makeQuery(id+"F5.opExtrude","CAP_FACE",FACE,{"disambiguationData":[OSD([subQ11,subQ10,subQ5,subQ4,subQ2,subQ1])],"isStart":true})]}),makeQuery(id+"F6.opExtrude","CAP_FACE",FACE,{"disambiguationData":[OSD([subQ9,subQ8,subQ7,subQ6,subQ5,subQ4,subQ3,subQ2,subQ1,subQ0])],"isStart":true})]});}
            var sketch = newSketch(context, id + "F13", { "sketchPlane" : qUnion([Q0])});
            skLineSegment(sketch, "E34", {"start": v(-58.8, -114.75) * mm, "end": v(-58.8, -116.93) * mm});
            skLineSegment(sketch, "E35", {"start": v(-29.19, -118.29) * mm, "end": v(-29.19, -120.29) * mm});
            skLineSegment(sketch, "E36", {"start": v(29.19, -118.29) * mm, "end": v(29.19, -120.29) * mm});
            skLineSegment(sketch, "E37", {"start": v(58.8, -114.75) * mm, "end": v(58.8, -116.93) * mm});
            skSolve(sketch);
        }
        {
            var Q0;
            {var subQ0=sQuery(id+"F13.wireOp",EDGE,"E34");Q0=makeQuery(id+"F13.imprint","IMPRINT",FACE,{"disambiguationData":[TD([[makeQuery(id+"F13.imprint","IMPRINT",EDGE,{"derivedFrom":subQ0}),1.0]])]});}
            extrude(context, id + "F14", {"entities" : qUnion([Q0]), "operationType" : NewBodyOperationType.REMOVE, "endBound" : BoundingType.SYMMETRIC, "oppositeDirection" : true, "depth" : 27 * mm, "offsetDistance" : 25 * mm});
        }
        {
            var Q0;
            {var subQ0=sQuery(id+"F13.wireOp",EDGE,"E36");Q0=makeQuery(id+"F13.imprint","IMPRINT",FACE,{"disambiguationData":[TD([[makeQuery(id+"F13.imprint","IMPRINT",EDGE,{"derivedFrom":subQ0}),1.0]])]});}
            extrude(context, id + "F15", {"entities" : qUnion([Q0]), "operationType" : NewBodyOperationType.REMOVE, "endBound" : BoundingType.SYMMETRIC, "oppositeDirection" : true, "depth" : 27 * mm, "offsetDistance" : 25 * mm});
        }
    });
